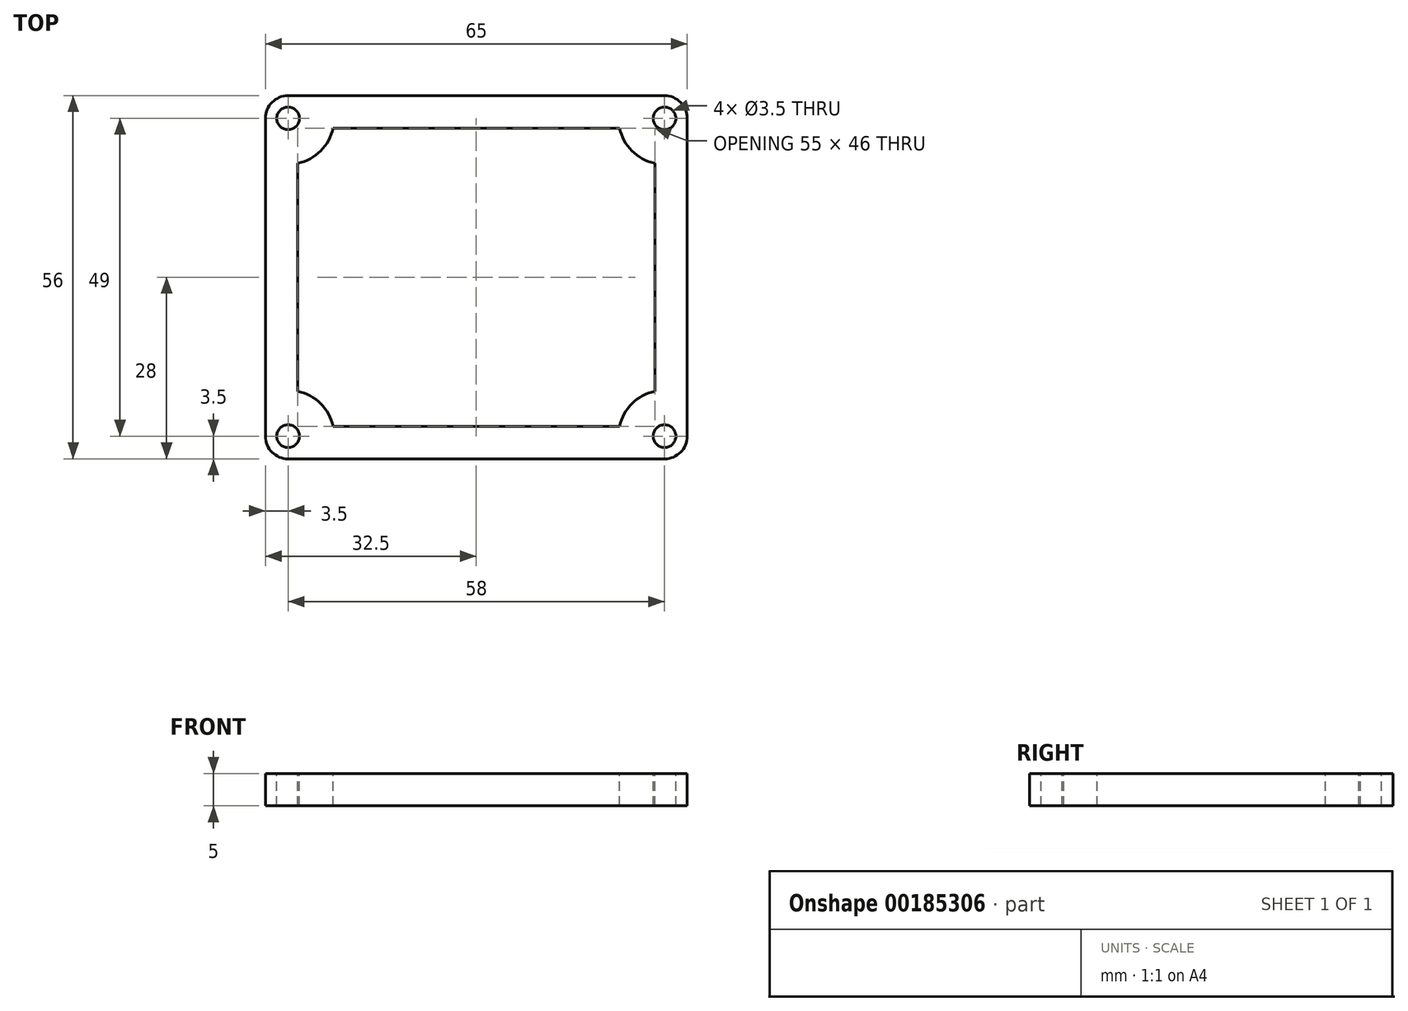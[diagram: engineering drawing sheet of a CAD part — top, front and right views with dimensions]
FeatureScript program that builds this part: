
annotation { "Feature Type Name" : "Feature", "Feature Type Description" : "" }
export const myFeature = defineFeature(function(context is Context, id is Id, definition is map)
    precondition{}
    {
        {
            var Q0;
            Q0=qCreatedBy(makeId("Top.planeOp"),FACE);
            var sketch = newSketch(context, id + "F0", { "sketchPlane" : qUnion([Q0])});
            skLineSegment(sketch, "E0.bottom", {"start": v(29, -28) * mm, "end": v(-29, -28) * mm});
            skLineSegment(sketch, "E0.top", {"start": v(29, 28) * mm, "end": v(-29, 28) * mm});
            skLineSegment(sketch, "E0.left", {"start": v(32.5, -24.5) * mm, "end": v(32.5, 24.5) * mm});
            skLineSegment(sketch, "E0.right", {"start": v(-32.5, -24.5) * mm, "end": v(-32.5, 24.5) * mm});
            skPoint(sketch, "E0.middle", {"position": v(0, 0) * mm});
            skPoint(sketch, "E1.visualSharp", {"position": v(-32.5, 28) * mm});
            skArc(sketch, "E1.filletArc", {"start": v(-29, 28) * mm, "mid": v(-31.47, 26.97) * mm, "end": v(-32.5, 24.5) * mm});
            skPoint(sketch, "E2.visualSharp", {"position": v(32.5, 28) * mm});
            skArc(sketch, "E2.filletArc", {"start": v(32.5, 24.5) * mm, "mid": v(31.47, 26.97) * mm, "end": v(29, 28) * mm});
            skPoint(sketch, "E3.visualSharp", {"position": v(32.5, -28) * mm});
            skArc(sketch, "E3.filletArc", {"start": v(29, -28) * mm, "mid": v(31.47, -26.97) * mm, "end": v(32.5, -24.5) * mm});
            skPoint(sketch, "E4.visualSharp", {"position": v(-32.5, -28) * mm});
            skArc(sketch, "E4.filletArc", {"start": v(-32.5, -24.5) * mm, "mid": v(-31.47, -26.97) * mm, "end": v(-29, -28) * mm});
            skSolve(sketch);
        }
        {
            var Q0;
            Q0 = qSketchRegion(id + "F0", true);
            extrude(context, id + "F1", {"entities" : qUnion([Q0]), "depth" : 5 * mm});
        }
        {
            var Q0;
            Q0=makeQuery(id+"F1.opExtrude","CAP_FACE",FACE,{"disambiguationData":[OSD([sQuery(id+"F0.wireOp",EDGE,"E0.bottom"),sQuery(id+"F0.wireOp",EDGE,"E0.top"),sQuery(id+"F0.wireOp",EDGE,"E0.left"),sQuery(id+"F0.wireOp",EDGE,"E0.right"),sQuery(id+"F0.wireOp",EDGE,"E1.filletArc"),sQuery(id+"F0.wireOp",EDGE,"E2.filletArc"),sQuery(id+"F0.wireOp",EDGE,"E3.filletArc"),sQuery(id+"F0.wireOp",EDGE,"E4.filletArc")])],"isStart":false});
            var sketch = newSketch(context, id + "F2", { "sketchPlane" : qUnion([Q0])});
            skCircle(sketch, "E5", {"center": v(-29, 24.5) * mm, "radius": 1.75 * mm});
            skCircle(sketch, "E6", {"center": v(29, 24.5) * mm, "radius": 1.75 * mm});
            skCircle(sketch, "E7", {"center": v(29, -24.5) * mm, "radius": 1.75 * mm});
            skCircle(sketch, "E8", {"center": v(-29, -24.5) * mm, "radius": 1.75 * mm});
            skSolve(sketch);
        }
        {
            var Q0;
            Q0 = qSketchRegion(id + "F2", true);
            extrude(context, id + "F3", {"entities" : qUnion([Q0]), "operationType" : NewBodyOperationType.REMOVE, "oppositeDirection" : true, "depth" : 5 * mm});
        }
        {
            var Q0;
            Q0=makeQuery(id+"F1.opExtrude","CAP_FACE",FACE,{"disambiguationData":[OSD([sQuery(id+"F0.wireOp",EDGE,"E0.bottom"),sQuery(id+"F0.wireOp",EDGE,"E0.top"),sQuery(id+"F0.wireOp",EDGE,"E0.left"),sQuery(id+"F0.wireOp",EDGE,"E0.right"),sQuery(id+"F0.wireOp",EDGE,"E1.filletArc"),sQuery(id+"F0.wireOp",EDGE,"E2.filletArc"),sQuery(id+"F0.wireOp",EDGE,"E3.filletArc"),sQuery(id+"F0.wireOp",EDGE,"E4.filletArc")])],"isStart":false});
            var sketch = newSketch(context, id + "F4", { "sketchPlane" : qUnion([Q0])});
            skLineSegment(sketch, "E9", {"start": v(-22.07, 23) * mm, "end": v(22.07, 23) * mm});
            skLineSegment(sketch, "E10", {"start": v(22.07, -23) * mm, "end": v(-22.07, -23) * mm});
            skArc(sketch, "E11", {"start": v(22.07, -23) * mm, "mid": v(23.98, -19.48) * mm, "end": v(27.5, -17.57) * mm});
            skArc(sketch, "E12", {"start": v(22.07, 23) * mm, "mid": v(23.98, 19.48) * mm, "end": v(27.5, 17.57) * mm});
            skLineSegment(sketch, "E13", {"start": v(27.5, -17.57) * mm, "end": v(27.5, 17.57) * mm});
            skArc(sketch, "E14", {"start": v(-22.07, -23) * mm, "mid": v(-23.98, -19.48) * mm, "end": v(-27.5, -17.57) * mm});
            skArc(sketch, "E15", {"start": v(-22.07, 23) * mm, "mid": v(-23.98, 19.48) * mm, "end": v(-27.5, 17.57) * mm});
            skLineSegment(sketch, "E16", {"start": v(-27.5, 17.57) * mm, "end": v(-27.5, -17.57) * mm});
            skSolve(sketch);
        }
        {
            var Q0;
            Q0 = qSketchRegion(id + "F4", true);
            extrude(context, id + "F5", {"entities" : qUnion([Q0]), "operationType" : NewBodyOperationType.REMOVE, "oppositeDirection" : true, "depth" : 5 * mm});
        }
    });
